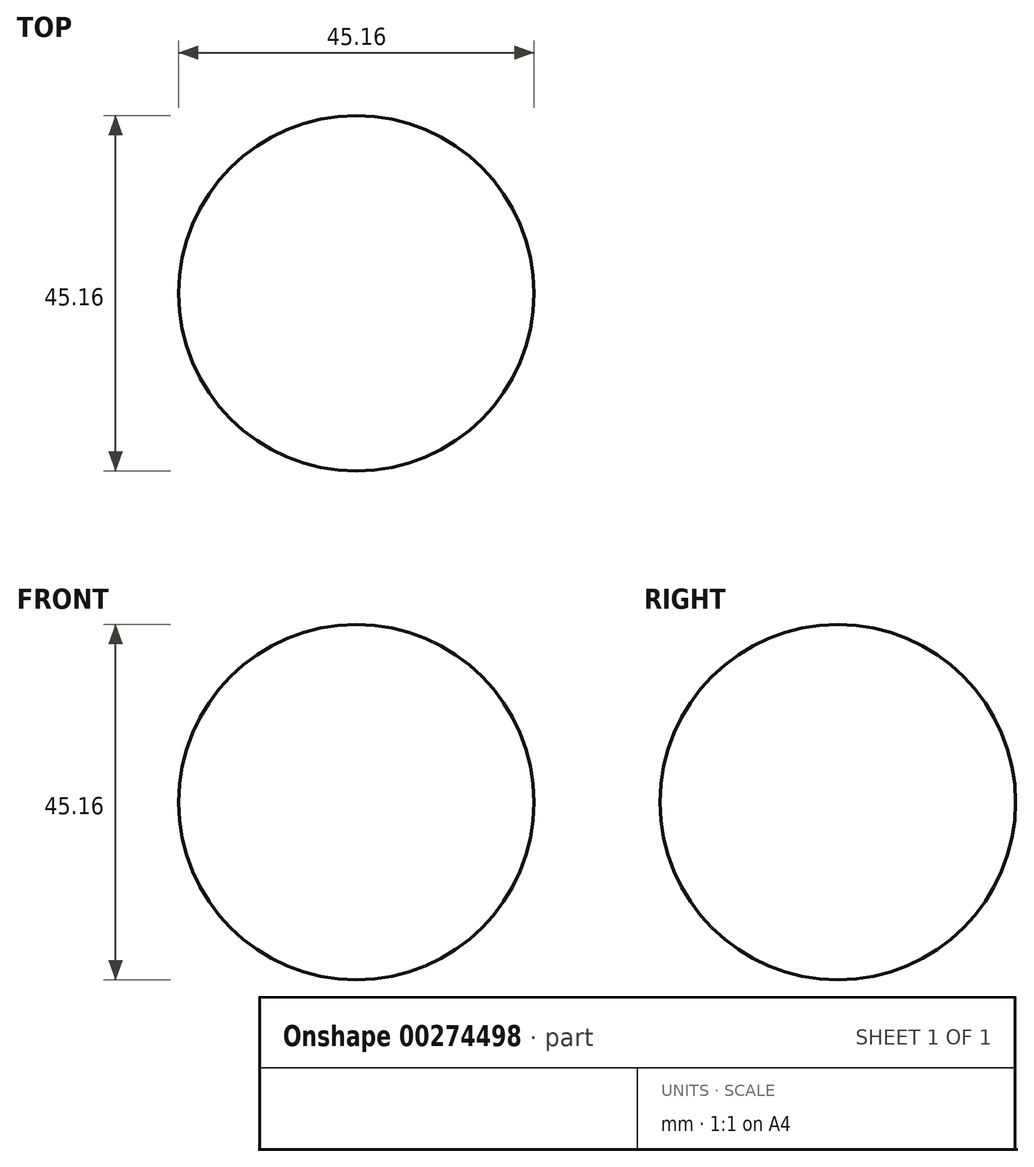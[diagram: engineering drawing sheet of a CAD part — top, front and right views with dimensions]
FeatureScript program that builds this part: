
annotation { "Feature Type Name" : "Feature", "Feature Type Description" : "" }
export const myFeature = defineFeature(function(context is Context, id is Id, definition is map)
    precondition{}
    {
        {
            var Q0;
            Q0=qCreatedBy(makeId("Front.planeOp"),FACE);
            var sketch = newSketch(context, id + "F0", { "sketchPlane" : qUnion([Q0])});
            skArc(sketch, "E0", {"start": v(0, 22.58) * mm, "mid": v(-22.58, 0) * mm, "end": v(0, -22.58) * mm});
            skLineSegment(sketch, "E1", {"start": v(0, 22.58) * mm, "end": v(0, -22.58) * mm});
            skSolve(sketch);
        }
        {
            var Q0;
            Q0=sQuery(id+"F0.wireOp",EDGE,"E0");
            var Q1;
            Q1=sQuery(id+"F0.wireOp",EDGE,"E1");
            revolve(context, id + "F1", {"bodyType" : ToolBodyType.SURFACE, "surfaceEntities" : qUnion([Q0]), "axis" : qUnion([Q1]), "revolveType" : RevolveType.FULL});
        }
    });
